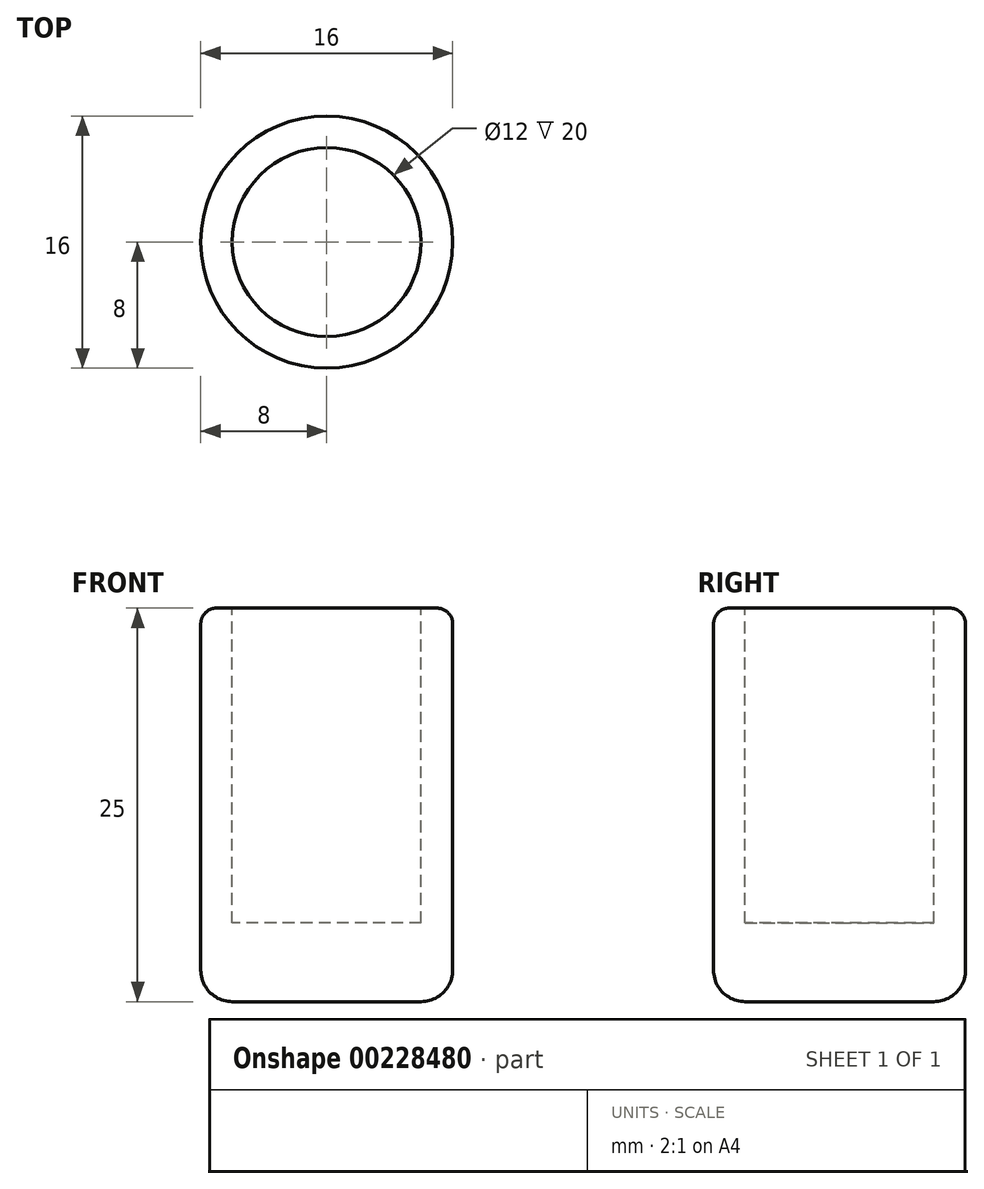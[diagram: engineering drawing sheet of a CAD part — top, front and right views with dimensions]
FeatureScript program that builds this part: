
annotation { "Feature Type Name" : "Feature", "Feature Type Description" : "" }
export const myFeature = defineFeature(function(context is Context, id is Id, definition is map)
    precondition{}
    {
        {
            var Q0;
            Q0=qCreatedBy(makeId("Top.planeOp"),FACE);
            var sketch = newSketch(context, id + "F0", { "sketchPlane" : qUnion([Q0])});
            skCircle(sketch, "E0", {"center": v(0, 0) * mm, "radius": 8 * mm});
            skSolve(sketch);
        }
        {
            var Q0;
            Q0=makeQuery(id+"F0.imprint","IMPRINT",FACE,{"disambiguationData":[TD([[makeQuery(id+"F0.imprint","IMPRINT",EDGE,{"derivedFrom":sQuery(id+"F0.wireOp",EDGE,"E0")}),1.0]])]});
            extrude(context, id + "F1", {"entities" : qUnion([Q0]), "depth" : 25 * mm, "offsetDistance" : 25 * mm});
        }
        {
            var Q0;
            Q0=makeQuery(id+"F1.opExtrude","CAP_EDGE",EDGE,{"disambiguationData":[OSD([sQuery(id+"F0.wireOp",EDGE,"E0")])],"isStart":true});
            fillet(context, id + "F2", {"entities" : qUnion([Q0]), "radius" : 2 * mm, "tangentPropagation" : true, "allowEdgeOverflow" : false});
        }
        {
            var Q0;
            Q0=makeQuery(id+"F1.opExtrude","CAP_FACE",FACE,{"disambiguationData":[OSD([sQuery(id+"F0.wireOp",EDGE,"E0")])],"isStart":false});
            var sketch = newSketch(context, id + "F3", { "sketchPlane" : qUnion([Q0])});
            skCircle(sketch, "E1", {"center": v(0, 0) * mm, "radius": 6 * mm});
            skSolve(sketch);
        }
        {
            var Q0;
            Q0=makeQuery(id+"F3.imprint","IMPRINT",FACE,{"disambiguationData":[TD([[makeQuery(id+"F3.imprint","IMPRINT",EDGE,{"derivedFrom":sQuery(id+"F3.wireOp",EDGE,"E1")}),1.0]])]});
            extrude(context, id + "F4", {"entities" : qUnion([Q0]), "operationType" : NewBodyOperationType.REMOVE, "oppositeDirection" : true, "depth" : 20 * mm, "offsetDistance" : 25 * mm});
        }
        {
            var Q0;
            Q0=makeQuery(id+"F1.opExtrude","CAP_EDGE",EDGE,{"disambiguationData":[OSD([sQuery(id+"F0.wireOp",EDGE,"E0")])],"isStart":false});
            fillet(context, id + "F5", {"entities" : qUnion([Q0]), "radius" : 1 * mm, "tangentPropagation" : true, "allowEdgeOverflow" : false});
        }
    });
